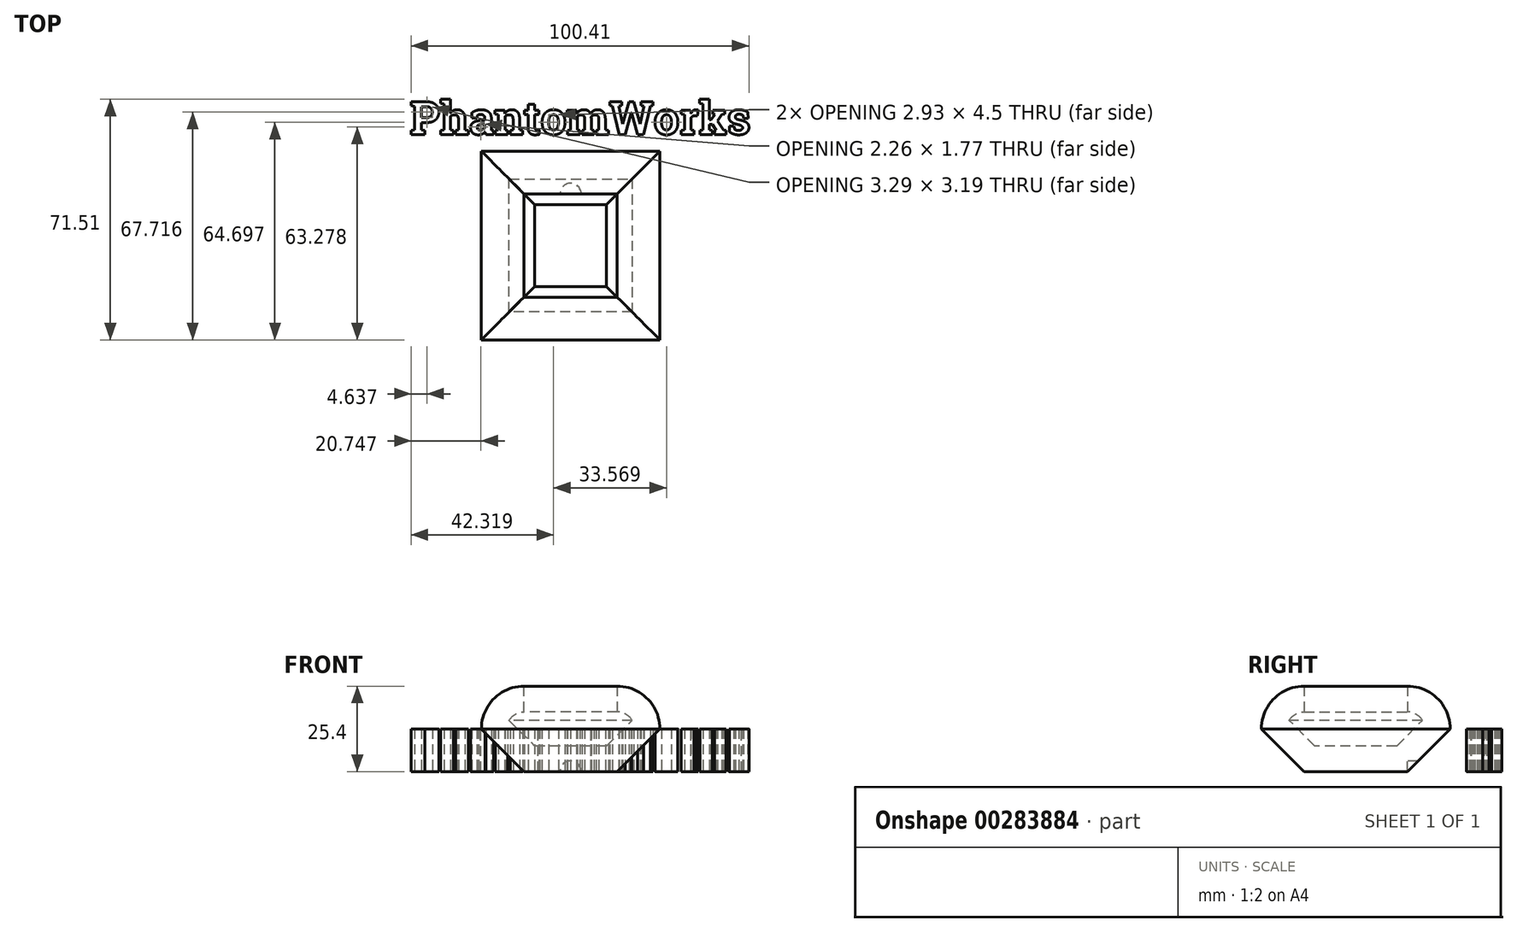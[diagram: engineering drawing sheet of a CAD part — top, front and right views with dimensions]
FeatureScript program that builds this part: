
annotation { "Feature Type Name" : "Feature", "Feature Type Description" : "" }
export const myFeature = defineFeature(function(context is Context, id is Id, definition is map)
    precondition{}
    {
        {
            var Q0;
            Q0=qCreatedBy(makeId("Top.planeOp"),FACE);
            var sketch = newSketch(context, id + "F0", { "sketchPlane" : qUnion([Q0])});
            skLineSegment(sketch, "E0.bottom", {"start": v(26.54, 28.06) * mm, "end": v(-26.54, 28.06) * mm});
            skLineSegment(sketch, "E0.top", {"start": v(26.54, -28.06) * mm, "end": v(-26.54, -28.06) * mm});
            skLineSegment(sketch, "E0.left", {"start": v(26.54, 28.06) * mm, "end": v(26.54, -28.06) * mm});
            skLineSegment(sketch, "E0.right", {"start": v(-26.54, 28.06) * mm, "end": v(-26.54, -28.06) * mm});
            skPoint(sketch, "E0.middle", {"position": v(0, 0) * mm});
            skSolve(sketch);
        }
        {
            var Q0;
            Q0=makeQuery(id+"F0.imprint","IMPRINT",FACE,{"disambiguationData":[TD([[makeQuery(id+"F0.imprint","IMPRINT",EDGE,{"derivedFrom":sQuery(id+"F0.wireOp",EDGE,"E0.bottom")}),1.0]])]});
            extrude(context, id + "F1", {"entities" : qUnion([Q0]), "depth" : 25.4 * mm});
        }
        {
            var Q0;
            Q0=makeQuery(id+"F1.opExtrude","CAP_EDGE",EDGE,{"disambiguationData":[OSD([sQuery(id+"F0.wireOp",EDGE,"E0.right")])],"isStart":false});
            var Q1;
            Q1=makeQuery(id+"F1.opExtrude","CAP_EDGE",EDGE,{"disambiguationData":[OSD([sQuery(id+"F0.wireOp",EDGE,"E0.top")])],"isStart":false});
            var Q2;
            Q2=makeQuery(id+"F1.opExtrude","CAP_EDGE",EDGE,{"disambiguationData":[OSD([sQuery(id+"F0.wireOp",EDGE,"E0.left")])],"isStart":false});
            var Q3;
            Q3=makeQuery(id+"F1.opExtrude","CAP_EDGE",EDGE,{"disambiguationData":[OSD([sQuery(id+"F0.wireOp",EDGE,"E0.bottom")])],"isStart":false});
            fillet(context, id + "F2", {"entities" : qUnion([Q0, Q1, Q2, Q3]), "radius" : 12.7 * mm, "tangentPropagation" : true, "allowEdgeOverflow" : false});
        }
        {
            var Q0;
            Q0=makeQuery(id+"F1.opExtrude","CAP_EDGE",EDGE,{"disambiguationData":[OSD([sQuery(id+"F0.wireOp",EDGE,"E0.left")])],"isStart":true});
            var Q1;
            Q1=makeQuery(id+"F1.opExtrude","CAP_EDGE",EDGE,{"disambiguationData":[OSD([sQuery(id+"F0.wireOp",EDGE,"E0.top")])],"isStart":true});
            var Q2;
            Q2=makeQuery(id+"F1.opExtrude","CAP_EDGE",EDGE,{"disambiguationData":[OSD([sQuery(id+"F0.wireOp",EDGE,"E0.bottom")])],"isStart":true});
            var Q3;
            Q3=makeQuery(id+"F1.opExtrude","CAP_EDGE",EDGE,{"disambiguationData":[OSD([sQuery(id+"F0.wireOp",EDGE,"E0.right")])],"isStart":true});
            chamfer(context, id + "F3", {"entities" : qUnion([Q0, Q1, Q2, Q3]), "width" : 12.7 * mm, "tangentPropagation" : true});
        }
        {
            var Q0;
            Q0=makeQuery(id+"F1.opExtrude","CAP_FACE",FACE,{"disambiguationData":[OSD([sQuery(id+"F0.wireOp",EDGE,"E0.bottom"),sQuery(id+"F0.wireOp",EDGE,"E0.top"),sQuery(id+"F0.wireOp",EDGE,"E0.left"),sQuery(id+"F0.wireOp",EDGE,"E0.right")])],"isStart":false});
            shell(context, id + "F4", {"entities" : qUnion([Q0]), "thickness" : 7.62 * mm});
        }
        {
            var Q0;
            Q0=makeQuery(id+"F4.opShell","OFFSET_FACE",FACE,{"disambiguationData":[OSD([sQuery(id+"F0.wireOp",EDGE,"E0.bottom"),sQuery(id+"F0.wireOp",EDGE,"E0.top"),sQuery(id+"F0.wireOp",EDGE,"E0.left"),sQuery(id+"F0.wireOp",EDGE,"E0.right")])]});
            var sketch = newSketch(context, id + "F5", { "sketchPlane" : qUnion([Q0])});
            skPoint(sketch, "E1", {"position": v(0, 0) * mm});
            skSolve(sketch);
        }
        {
            var Q0;
            Q0=sQuery(id+"F5.wireOp",VERTEX,"E1");
            var Q1;
            Q1=makeQuery(id+"F1.opExtrude","SWEPT_BODY",BODY,{"disambiguationData":[OSD([sQuery(id+"F0.wireOp",EDGE,"E0.bottom"),sQuery(id+"F0.wireOp",EDGE,"E0.top"),sQuery(id+"F0.wireOp",EDGE,"E0.left"),sQuery(id+"F0.wireOp",EDGE,"E0.right")])]});
            hole(context, id + "F6", {"style" : HoleStyle.C_BORE, "endStyle" : HoleEndStyle.THROUGH, "holeDiameter" : 5.08 * mm, "cBoreDiameter" : 6.35 * mm, "cBoreDepth" : 6.35 * mm, "tappedDepth" : 12.7 * mm, "tapClearance" : 3, "locations" : qUnion([Q0]), "scope" : qUnion([Q1])});
        }
        {
            var Q0;
            Q0=qCreatedBy(makeId("Top.planeOp"),FACE);
            var sketch = newSketch(context, id + "F7", { "sketchPlane" : qUnion([Q0])});
            skText(sketch, "E2", { "text": "PhantomWorks", "fontName": "RobotoSlab-Bold.ttf"});
            const initialGuessF7  = {"E2": [-0.04777, 0.03303, 1, 0, 0.00985]};
            skSetInitialGuess(sketch, initialGuessF7);
            skSolve(sketch);
        }
        {
            var Q0;
            Q0 = qSketchRegion(id + "F7", true);
            extrude(context, id + "F8", {"entities" : qUnion([Q0]), "depth" : 12.7 * mm});
        }
    });
